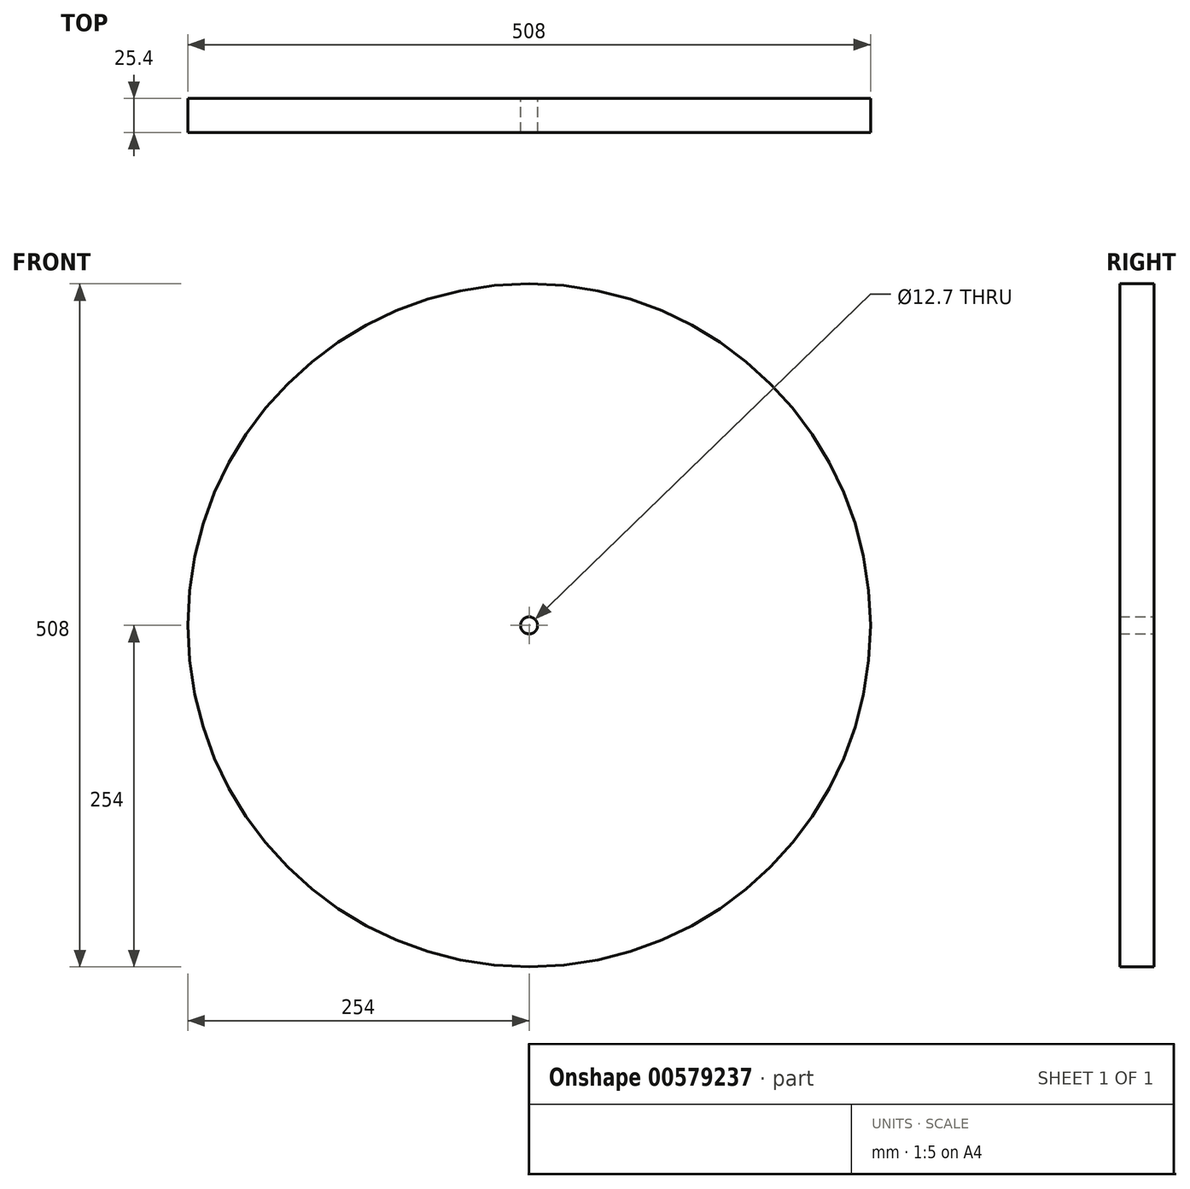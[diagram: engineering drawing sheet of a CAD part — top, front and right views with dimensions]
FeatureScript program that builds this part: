
annotation { "Feature Type Name" : "Feature", "Feature Type Description" : "" }
export const myFeature = defineFeature(function(context is Context, id is Id, definition is map)
    precondition{}
    {
        {
            var Q0;
            Q0=qCreatedBy(makeId("Front.planeOp"),FACE);
            var sketch = newSketch(context, id + "F0", { "sketchPlane" : qUnion([Q0])});
            skCircle(sketch, "E0", {"center": v(0, 0) * mm, "radius": 6.35 * mm});
            skCircle(sketch, "E1", {"center": v(0, 0) * mm, "radius": 254 * mm});
            skSolve(sketch);
        }
        {
            var Q0;
            Q0=makeQuery(id+"F0.imprint","IMPRINT",FACE,{"disambiguationData":[TD([[makeQuery(id+"F0.imprint","IMPRINT",EDGE,{"derivedFrom":sQuery(id+"F0.wireOp",EDGE,"E0")}),-1.0]])]});
            extrude(context, id + "F1", {"entities" : qUnion([Q0]), "depth" : 25.4 * mm, "offsetDistance" : 25.4 * mm});
        }
    });
